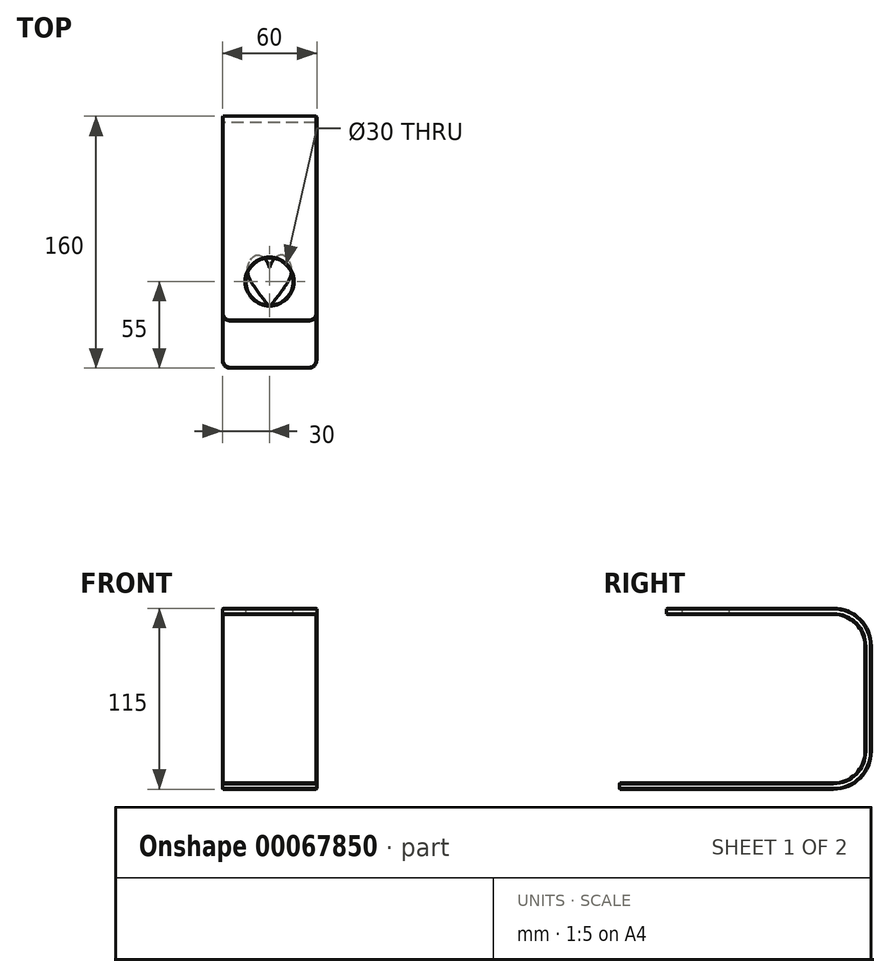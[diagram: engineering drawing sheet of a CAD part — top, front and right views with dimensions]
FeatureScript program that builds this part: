
annotation { "Feature Type Name" : "Feature", "Feature Type Description" : "" }
export const myFeature = defineFeature(function(context is Context, id is Id, definition is map)
    precondition{}
    {
        {
            var Q0;
            Q0=qCreatedBy(makeId("Right.planeOp"),FACE);
            var sketch = newSketch(context, id + "F0", { "sketchPlane" : qUnion([Q0])});
            skLineSegment(sketch, "E0", {"start": v(0, 0) * mm, "end": v(160, 0) * mm});
            skLineSegment(sketch, "E1", {"start": v(160, 0) * mm, "end": v(160, 115) * mm});
            skLineSegment(sketch, "E2", {"start": v(160, 115) * mm, "end": v(30, 115) * mm});
            skLineSegment(sketch, "E3.0", {"start": v(156, 111) * mm, "end": v(30, 111) * mm});
            skLineSegment(sketch, "E3.1", {"start": v(156, 4) * mm, "end": v(156, 111) * mm});
            skLineSegment(sketch, "E3.2", {"start": v(0, 4) * mm, "end": v(156, 4) * mm});
            skLineSegment(sketch, "E4", {"start": v(30, 115) * mm, "end": v(30, 111) * mm});
            skLineSegment(sketch, "E5", {"start": v(0, 4) * mm, "end": v(0, 0) * mm});
            skSolve(sketch);
        }
        {
            var Q0;
            Q0 = qSketchRegion(id + "F0", true);
            extrude(context, id + "F1", {"entities" : qUnion([Q0]), "depth" : 60 * mm});
        }
        {
            var Q0;
            Q0=makeQuery(id+"F1.opExtrude","SWEPT_EDGE",EDGE,{"disambiguationData":[OSD([sQuery(id+"F0.wireOp",EDGE,"E3.0"),sQuery(id+"F0.wireOp",EDGE,"E3.1")])]});
            var Q1;
            Q1=makeQuery(id+"F1.opExtrude","SWEPT_EDGE",EDGE,{"disambiguationData":[OSD([sQuery(id+"F0.wireOp",EDGE,"E3.1"),sQuery(id+"F0.wireOp",EDGE,"E3.2")])]});
            fillet(context, id + "F2", {"entities" : qUnion([Q0, Q1]), "radius" : 20 * mm, "tangentPropagation" : true, "allowEdgeOverflow" : false});
        }
        {
            var Q0;
            Q0=makeQuery(id+"F1.opExtrude","SWEPT_EDGE",EDGE,{"disambiguationData":[OSD([sQuery(id+"F0.wireOp",EDGE,"E1"),sQuery(id+"F0.wireOp",EDGE,"E2")])]});
            var Q1;
            Q1=makeQuery(id+"F1.opExtrude","SWEPT_EDGE",EDGE,{"disambiguationData":[OSD([sQuery(id+"F0.wireOp",EDGE,"E0"),sQuery(id+"F0.wireOp",EDGE,"E1")])]});
            fillet(context, id + "F3", {"entities" : qUnion([Q0, Q1]), "radius" : 24 * mm, "tangentPropagation" : true, "allowEdgeOverflow" : false});
        }
        {
            var Q0;
            Q0=makeQuery(id+"F1.opExtrude","CAP_EDGE",EDGE,{"disambiguationData":[OSD([sQuery(id+"F0.wireOp",EDGE,"E4")])],"isStart":true});
            var Q1;
            Q1=makeQuery(id+"F1.opExtrude","CAP_EDGE",EDGE,{"disambiguationData":[OSD([sQuery(id+"F0.wireOp",EDGE,"E4")])],"isStart":false});
            var Q2;
            Q2=makeQuery(id+"F1.opExtrude","CAP_EDGE",EDGE,{"disambiguationData":[OSD([sQuery(id+"F0.wireOp",EDGE,"E5")])],"isStart":true});
            var Q3;
            Q3=makeQuery(id+"F1.opExtrude","CAP_EDGE",EDGE,{"disambiguationData":[OSD([sQuery(id+"F0.wireOp",EDGE,"E5")])],"isStart":false});
            fillet(context, id + "F4", {"entities" : qUnion([Q0, Q1, Q2, Q3]), "radius" : 5 * mm, "tangentPropagation" : true, "allowEdgeOverflow" : false});
        }
        {
            var Q0;
            Q0=makeQuery(id+"F1.opExtrude","SWEPT_FACE",FACE,{"disambiguationData":[OSD([sQuery(id+"F0.wireOp",EDGE,"E2")])]});
            var sketch = newSketch(context, id + "F5", { "sketchPlane" : qUnion([Q0])});
            skLineSegment(sketch, "E6", {"start": v(30, 30) * mm, "end": v(30, 55) * mm, "construction": true});
            skCircle(sketch, "E7", {"center": v(30, 55) * mm, "radius": 15 * mm});
            skSolve(sketch);
        }
        {
            var Q0;
            Q0 = qSketchRegion(id + "F5", true);
            extrude(context, id + "F6", {"entities" : qUnion([Q0]), "operationType" : NewBodyOperationType.REMOVE, "endBound" : BoundingType.UP_TO_NEXT, "oppositeDirection" : true, "depth" : 25 * mm});
        }
        {
            var Q0;
            Q0=makeQuery(id+"F6.boolean.opBoolean","COPY",FACE,{"derivedFrom":makeQuery(id+"F6.opExtrude","SWEPT_FACE",FACE,{"disambiguationData":[OSD([sQuery(id+"F5.wireOp",EDGE,"E7")])]})});
            var Q1;
            Q1=makeQuery(id+"F1.opExtrude","CAP_FACE",FACE,{"disambiguationData":[OSD([sQuery(id+"F0.wireOp",EDGE,"E0"),sQuery(id+"F0.wireOp",EDGE,"E1"),sQuery(id+"F0.wireOp",EDGE,"E2"),sQuery(id+"F0.wireOp",EDGE,"E3.0"),sQuery(id+"F0.wireOp",EDGE,"E3.1"),sQuery(id+"F0.wireOp",EDGE,"E3.2"),sQuery(id+"F0.wireOp",EDGE,"E4"),sQuery(id+"F0.wireOp",EDGE,"E5")])],"isStart":false});
            chamfer(context, id + "F7", {"entities" : qUnion([Q0, Q1]), "width" : .5 * mm, "tangentPropagation" : true});
        }
        {
            var Q0;
            Q0=makeQuery(id+"F1.opExtrude","SWEPT_FACE",FACE,{"disambiguationData":[OSD([sQuery(id+"F0.wireOp",EDGE,"E3.2")])]});
            var sketch = newSketch(context, id + "F8", { "sketchPlane" : qUnion([Q0])});
            skFitSpline(sketch, "E8", {"points": [v(30, 38.6) * mm, v(44.04, 62.8) * mm, v(37.59, 71.87) * mm, v(30, 62.78) * mm], "startDerivative": vector(54.78, 76.78) * mm, "endDerivative": vector(-5.46, -48.05) * mm});
            skLineSegment(sketch, "E9", {"start": v(30, 62.78) * mm, "end": v(30, 38.6) * mm, "construction": true});
            skLineSegment(sketch, "E10", {"start": v(30, 38.6) * mm, "end": v(30, 0.5) * mm, "construction": true});
            skFitSpline(sketch, "E11.MirrorCS", {"points": [v(30, 38.6) * mm, v(15.96, 62.8) * mm, v(22.41, 71.87) * mm, v(30, 62.78) * mm], "startDerivative": vector(-54.78, 76.78) * mm, "endDerivative": vector(5.46, -48.05) * mm});
            skSolve(sketch);
        }
        {
            var Q0;
            Q0=makeQuery(id+"F8.imprint","IMPRINT",FACE,{"disambiguationData":[TD([[makeQuery(id+"F8.imprint","IMPRINT",EDGE,{"derivedFrom":sQuery(id+"F8.wireOp",EDGE,"E8")}),1.0]])]});
            var Q1;
            Q1=sQuery(id+"F8.wireOp",EDGE,"E11.MirrorCS");
            var Q2;
            Q2=sQuery(id+"F8.wireOp",EDGE,"E8");
            extrude(context, id + "F9", {"entities" : qUnion([Q0]), "operationType" : NewBodyOperationType.REMOVE, "surfaceEntities" : qUnion([Q1, Q2]), "oppositeDirection" : true, "depth" : .5 * mm});
        }
        {
            var Q0;
            {var subQ0=sQuery(id+"F8.wireOp",EDGE,"E11.MirrorCS");var subQ1=sQuery(id+"F8.wireOp",EDGE,"E8");Q0=makeQuery(id+"F9.boolean.opBoolean","COPY",EDGE,{"derivedFrom":makeQuery(id+"F9.opExtrude","SWEPT_EDGE",EDGE,{"disambiguationData":[OSD([subQ1,subQ0]),TDD([makeQuery(id+"F8.imprint","INTERSECT",VERTEX,{"disambiguationData":[OD(1.0)],"derivedFrom":[subQ1,subQ0]})])]})});}
            var Q1;
            Q1=makeQuery(id+"F9.boolean.opBoolean","COPY",EDGE,{"derivedFrom":makeQuery(id+"F9.opExtrude","CAP_EDGE",EDGE,{"disambiguationData":[OSD([sQuery(id+"F8.wireOp",EDGE,"E8")])],"isStart":true})});
            var Q2;
            Q2=makeQuery(id+"F9.boolean.opBoolean","COPY",EDGE,{"derivedFrom":makeQuery(id+"F9.opExtrude","CAP_EDGE",EDGE,{"disambiguationData":[OSD([sQuery(id+"F8.wireOp",EDGE,"E11.MirrorCS")])],"isStart":true})});
            var Q3;
            {var subQ0=sQuery(id+"F8.wireOp",EDGE,"E11.MirrorCS");var subQ1=sQuery(id+"F8.wireOp",EDGE,"E8");Q3=makeQuery(id+"F9.boolean.opBoolean","COPY",EDGE,{"derivedFrom":makeQuery(id+"F9.opExtrude","SWEPT_EDGE",EDGE,{"disambiguationData":[OSD([subQ1,subQ0]),TDD([makeQuery(id+"F8.imprint","INTERSECT",VERTEX,{"disambiguationData":[OD(0.0)],"derivedFrom":[subQ1,subQ0]})])]})});}
            fillet(context, id + "F10", {"entities" : qUnion([Q0, Q1, Q2, Q3]), "radius" : .2 * mm, "tangentPropagation" : true, "allowEdgeOverflow" : false});
        }
    });
